# Revit family: Door-Exterior-Simpson-Nantucket-Quarter-Glass-Single
name_source: partatom
category: Doors
revit_build: Autodesk Revit Architecture 2012 (Build: 20110916_2132(x64)
units: mm (PartAtom-declared; Revit-internal decimal feet)

## types (63) — shared parameters
Assembly Code = B2030230
Construction Type = Wood
Frame = Wood - Simpson Doors - Douglas Fir
Frame Projection Ext. = 0' - 1"
Frame Projection Int. = 0' - 1"
Frame Type = Frame : Standard
Frame Width = 0' - 3"
Function = Exterior
Glass = Glass - Simpson Doors - Clear
Glass Options = http://simpsondoor.com
Horizontal Outside Muntin = No
Innerbond Double Hip-Raised Panel = No
Manufacturer = Simpsons Door Company
Number of Horizontal Muntins = 1
Ovolo Construction = Yes
Panel = Wood - Simpson Doors - Douglas Fir
Panel Stile Width = 0' - 5"
Product Documentation Link = http://www.simpsondoor.com
Product Page URL = http://www.simpsondoor.com
Thickness = 0' - 1 3/4"
Thickness Note = comes in 1 3/4" and 2 1/4" Thickness. Default is set to 1 3/4"
URL = http://www.simpsondoor.com
Vertical Outside Muntin = No
Wall Closure = By host
Wood Species = http://simpsondoor.com

## per-type parameters (varying)
| type | Bottom Rail Height | Description | Height | Middle Rail Height | Model | Muntin Width | Number of Panel Dividers | Number of Vertical Muntins | Panel Divider Width | Rough Height | Rough Width | Top Rail Height | Width | Window Height |
| 77662 Nantucket 36x80 Ovolo Flat Panel | 0' - 8 11/16" | Nantucket - Six Lite - Two Panel | 6' - 8" | 0' - 4 1/2" | 77662 | 0' - 0 3/8" | 1 | 2 | 0' - 3 1/2" | 6' - 10" | 3' - 4" | 0' - 4 15/16" | 3' - 0" | 1' - 6 1/2" |
| 77662 Nantucket 30x80 Ovolo Flat Panel | 0' - 8 11/16" | Nantucket - Six Lite - Two Panel | 6' - 8" | 0' - 4 1/2" | 77662 | 0' - 0 3/8" | 1 | 2 | 0' - 3 1/2" | 6' - 10" | 2' - 10" | 0' - 4 15/16" | 2' - 6" | 1' - 6 1/2" |
| 77662 Nantucket 32x80 Ovolo Flat Panel | 0' - 8 11/16" | Nantucket - Six Lite - Two Panel | 6' - 8" | 0' - 4 1/2" | 77662 | 0' - 0 3/8" | 1 | 2 | 0' - 3 1/2" | 6' - 10" | 3' - 0" | 0' - 4 15/16" | 2' - 8" | 1' - 6 1/2" |
| 77662 Nantucket 34x80 Ovolo Flat Panel | 0' - 8 11/16" | Nantucket - Six Lite - Two Panel | 6' - 8" | 0' - 4 1/2" | 77662 | 0' - 0 3/8" | 1 | 2 | 0' - 3 1/2" | 6' - 10" | 3' - 2" | 0' - 4 15/16" | 2' - 10" | 1' - 6 1/2" |
| 77662 Nantucket 38x80 Ovolo Flat Panel | 0' - 8 11/16" | Nantucket - Six Lite - Two Panel | 6' - 8" | 0' - 4 1/2" | 77662 | 0' - 0 3/8" | 1 | 2 | 0' - 3 1/2" | 6' - 10" | 3' - 6" | 0' - 4 15/16" | 3' - 2" | 1' - 6 1/2" |
| 77662 Nantucket 40x80 Ovolo Flat Panel | 0' - 8 11/16" | Nantucket - Six Lite - Two Panel | 6' - 8" | 0' - 4 1/2" | 77662 | 0' - 0 3/8" | 1 | 2 | 0' - 3 1/2" | 6' - 10" | 3' - 8" | 0' - 4 15/16" | 3' - 4" | 1' - 6 1/2" |
| 77662 Nantucket 42x80 Ovolo Flat Panel | 0' - 8 11/16" | Nantucket - Six Lite - Two Panel | 6' - 8" | 0' - 4 1/2" | 77662 | 0' - 0 3/8" | 1 | 2 | 0' - 3 1/2" | 6' - 10" | 3' - 10" | 0' - 4 15/16" | 3' - 6" | 1' - 6 1/2" |
| 77664 Nantucket 36x80 Ovolo Flat Panel | 0' - 8 11/16" | Nantucket - Six Lite - Two Panel | 6' - 8" | 0' - 4 1/2" | 77664 | 0' - 0 3/8" | 1 | 1 | 0' - 3 1/2" | 6' - 10" | 3' - 4" | 0' - 4 15/16" | 3' - 0" | 1' - 6 1/2" |
| 77664 Nantucket 30x80 Ovolo Flat Panel | 0' - 8 11/16" | Nantucket - Four Lite - Two Panel | 6' - 8" | 0' - 4 1/2" | 77664 | 0' - 0 3/8" | 1 | 1 | 0' - 3 1/2" | 6' - 10" | 2' - 10" | 0' - 4 15/16" | 2' - 6" | 1' - 6 1/2" |
| 77664 Nantucket 32x80 Ovolo Flat Panel | 0' - 8 11/16" | Nantucket - Four Lite - Two Panel | 6' - 8" | 0' - 4 1/2" | 77664 | 0' - 0 3/8" | 1 | 1 | 0' - 3 1/2" | 6' - 10" | 3' - 0" | 0' - 4 15/16" | 2' - 8" | 1' - 6 1/2" |
| 77664 Nantucket 34x80 Ovolo Flat Panel | 0' - 8 11/16" | Nantucket - Four Lite - Two Panel | 6' - 8" | 0' - 4 1/2" | 77664 | 0' - 0 3/8" | 1 | 1 | 0' - 3 1/2" | 6' - 10" | 3' - 2" | 0' - 4 15/16" | 2' - 10" | 1' - 6 1/2" |
| 77664 Nantucket 38x80 Ovolo Flat Panel | 0' - 8 11/16" | Nantucket - Four Lite - Two Panel | 6' - 8" | 0' - 4 1/2" | 77664 | 0' - 0 3/8" | 1 | 1 | 0' - 3 1/2" | 6' - 10" | 3' - 6" | 0' - 4 15/16" | 3' - 2" | 1' - 6 1/2" |
| 77664 Nantucket 40x80 Ovolo Flat Panel | 0' - 8 11/16" | Nantucket - Four Lite - Two Panel | 6' - 8" | 0' - 4 1/2" | 77664 | 0' - 0 3/8" | 1 | 1 | 0' - 3 1/2" | 6' - 10" | 3' - 8" | 0' - 4 15/16" | 3' - 4" | 1' - 6 1/2" |
| 77664 Nantucket 42x80 Ovolo Flat Panel | 0' - 8 11/16" | Nantucket - Four Lite - Two Panel | 6' - 8" | 0' - 4 1/2" | 77664 | 0' - 0 3/8" | 1 | 1 | 0' - 3 1/2" | 6' - 10" | 3' - 10" | 0' - 4 15/16" | 3' - 6" | 1' - 6 1/2" |
| 77860 Nantucket 36x80 Ovolo Flat Panel | 0' - 8 11/16" | Nantucket - Six Lite - Three Panel | 6' - 8" | 0' - 5 1/2" | 77860 | 0' - 1 3/4" | 2 | 2 | 0' - 1 3/4" | 6' - 10" | 3' - 4" | 0' - 4 15/16" | 3' - 0" | 1' - 6 1/2" |
| 77860 Nantucket 30x80 Ovolo Flat Panel | 0' - 8 11/16" | Nantucket - Six Lite - Three Panel | 6' - 8" | 0' - 5 1/2" | 77860 | 0' - 1 3/4" | 2 | 2 | 0' - 1 3/4" | 6' - 10" | 2' - 10" | 0' - 4 15/16" | 2' - 6" | 1' - 6 1/2" |
| 77860 Nantucket 32x80 Ovolo Flat Panel | 0' - 8 11/16" | Nantucket - Six Lite - Three Panel | 6' - 8" | 0' - 5 1/2" | 77860 | 0' - 1 3/4" | 2 | 2 | 0' - 1 3/4" | 6' - 10" | 3' - 0" | 0' - 4 15/16" | 2' - 8" | 1' - 6 1/2" |
| 77860 Nantucket 34x80 Ovolo Flat Panel | 0' - 8 11/16" | Nantucket - Six Lite - Three Panel | 6' - 8" | 0' - 5 1/2" | 77860 | 0' - 1 3/4" | 2 | 2 | 0' - 1 3/4" | 6' - 10" | 3' - 2" | 0' - 4 15/16" | 2' - 10" | 1' - 6 1/2" |
| 77860 Nantucket 38x80 Ovolo Flat Panel | 0' - 8 11/16" | Nantucket - Six Lite - Three Panel | 6' - 8" | 0' - 5 1/2" | 77860 | 0' - 1 3/4" | 2 | 2 | 0' - 1 3/4" | 6' - 10" | 3' - 6" | 0' - 4 15/16" | 3' - 2" | 1' - 6 1/2" |
| 77860 Nantucket 40x80 Ovolo Flat Panel | 0' - 8 11/16" | Nantucket - Six Lite - Three Panel | 6' - 8" | 0' - 5 1/2" | 77860 | 0' - 1 3/4" | 2 | 2 | 0' - 1 3/4" | 6' - 10" | 3' - 8" | 0' - 4 15/16" | 3' - 4" | 1' - 6 1/2" |
| 77860 Nantucket 42x80 Ovolo Flat Panel | 0' - 8 11/16" | Nantucket - Six Lite - Three Panel | 6' - 8" | 0' - 5 1/2" | 77860 | 0' - 1 3/4" | 2 | 2 | 0' - 1 3/4" | 6' - 10" | 3' - 10" | 0' - 4 15/16" | 3' - 6" | 1' - 6 1/2" |
| 77662 Nantucket 36x84 Ovolo Flat Panel | 0' - 8 11/16" | Nantucket - Six Lite - Two Panel | 7' - 0" | 0' - 4 1/2" | 77662 | 0' - 0 3/8" | 1 | 2 | 0' - 3 1/2" | 7' - 2" | 3' - 4" | 0' - 4 15/16" | 3' - 0" | 1' - 6 1/2" |
| 77662 Nantucket 30x84 Ovolo Flat Panel | 0' - 10 11/16" | Nantucket - Six Lite - Two Panel | 7' - 0" | 0' - 4 1/2" | 77662 | 0' - 0 3/8" | 1 | 2 | 0' - 3 1/2" | 7' - 2" | 2' - 10" | 0' - 6 15/16" | 2' - 6" | 1' - 6 1/2" |
| 77662 Nantucket 32x84 Ovolo Flat Panel | 0' - 10 11/16" | Nantucket - Six Lite - Two Panel | 7' - 0" | 0' - 4 1/2" | 77662 | 0' - 0 3/8" | 1 | 2 | 0' - 3 1/2" | 7' - 2" | 3' - 0" | 0' - 6 15/16" | 2' - 8" | 1' - 6 1/2" |
| 77662 Nantucket 34x84 Ovolo Flat Panel | 0' - 10 11/16" | Nantucket - Six Lite - Two Panel | 7' - 0" | 0' - 4 1/2" | 77662 | 0' - 0 3/8" | 1 | 2 | 0' - 3 1/2" | 7' - 2" | 3' - 2" | 0' - 6 15/16" | 2' - 10" | 1' - 6 1/2" |
| 77662 Nantucket 38x84 Ovolo Flat Panel | 0' - 10 11/16" | Nantucket - Six Lite - Two Panel | 7' - 0" | 0' - 4 1/2" | 77662 | 0' - 0 3/8" | 1 | 2 | 0' - 3 1/2" | 7' - 2" | 3' - 6" | 0' - 6 15/16" | 3' - 2" | 1' - 6 1/2" |
| 77662 Nantucket 40x84 Ovolo Flat Panel | 0' - 10 11/16" | Nantucket - Six Lite - Two Panel | 7' - 0" | 0' - 4 1/2" | 77662 | 0' - 0 3/8" | 1 | 2 | 0' - 3 1/2" | 7' - 2" | 3' - 8" | 0' - 6 15/16" | 3' - 4" | 1' - 6 1/2" |
| 77662 Nantucket 42x84 Ovolo Flat Panel | 0' - 10 11/16" | Nantucket - Six Lite - Two Panel | 7' - 0" | 0' - 4 1/2" | 77662 | 0' - 0 3/8" | 1 | 2 | 0' - 3 1/2" | 7' - 2" | 3' - 10" | 0' - 6 15/16" | 3' - 6" | 1' - 6 1/2" |
| 77664 Nantucket 36x84 Ovolo Flat Panel | 0' - 10 11/16" | Nantucket - Four Lite - Two Panel | 7' - 0" | 0' - 4 1/2" | 77664 | 0' - 0 3/8" | 1 | 1 | 0' - 3 1/2" | 7' - 2" | 3' - 4" | 0' - 6 15/16" | 3' - 0" | 1' - 6 1/2" |
| 77664 Nantucket 30x84 Ovolo Flat Panel | 0' - 10 11/16" | Nantucket - Four Lite - Two Panel | 7' - 0" | 0' - 4 1/2" | 77664 | 0' - 0 3/8" | 1 | 1 | 0' - 3 1/2" | 7' - 2" | 2' - 10" | 0' - 6 15/16" | 2' - 6" | 1' - 6 1/2" |
| 77664 Nantucket 32x84 Ovolo Flat Panel | 0' - 10 11/16" | Nantucket - Four Lite - Two Panel | 7' - 0" | 0' - 4 1/2" | 77664 | 0' - 0 3/8" | 1 | 1 | 0' - 3 1/2" | 7' - 2" | 3' - 0" | 0' - 6 15/16" | 2' - 8" | 1' - 6 1/2" |
| 77664 Nantucket 34x84 Ovolo Flat Panel | 0' - 10 11/16" | Nantucket - Four Lite - Two Panel | 7' - 0" | 0' - 4 1/2" | 77664 | 0' - 0 3/8" | 1 | 1 | 0' - 3 1/2" | 7' - 2" | 3' - 2" | 0' - 6 15/16" | 2' - 10" | 1' - 6 1/2" |
| 77664 Nantucket 38x84 Ovolo Flat Panel | 0' - 10 11/16" | Nantucket - Four Lite - Two Panel | 7' - 0" | 0' - 4 1/2" | 77664 | 0' - 0 3/8" | 1 | 1 | 0' - 3 1/2" | 7' - 2" | 3' - 6" | 0' - 6 15/16" | 3' - 2" | 1' - 6 1/2" |
| 77664 Nantucket 40x84 Ovolo Flat Panel | 0' - 10 11/16" | Nantucket - Four Lite - Two Panel | 7' - 0" | 0' - 4 1/2" | 77664 | 0' - 0 3/8" | 1 | 1 | 0' - 3 1/2" | 7' - 2" | 3' - 8" | 0' - 6 15/16" | 3' - 4" | 1' - 6 1/2" |
| 77664 Nantucket 42x84 Ovolo Flat Panel | 0' - 10 11/16" | Nantucket - Four Lite - Two Panel | 7' - 0" | 0' - 4 1/2" | 77664 | 0' - 0 3/8" | 1 | 1 | 0' - 3 1/2" | 7' - 2" | 3' - 10" | 0' - 6 15/16" | 3' - 6" | 1' - 6 1/2" |
| 77860 Nantucket 36x84 Ovolo Flat Panel | 0' - 10 11/16" | Nantucket - Six Lite - Three Panel | 7' - 0" | 0' - 5 1/2" | 77860 | 0' - 1 3/4" | 2 | 2 | 0' - 1 3/4" | 7' - 2" | 3' - 4" | 0' - 6 15/16" | 3' - 0" | 1' - 6 1/2" |
| 77860 Nantucket 30x84 Ovolo Flat Panel | 0' - 10 11/16" | Nantucket - Six Lite - Three Panel | 7' - 0" | 0' - 5 1/2" | 77860 | 0' - 1 3/4" | 2 | 2 | 0' - 1 3/4" | 7' - 2" | 2' - 10" | 0' - 6 15/16" | 2' - 6" | 1' - 6 1/2" |
| 77860 Nantucket 32x84 Ovolo Flat Panel | 0' - 10 11/16" | Nantucket - Six Lite - Three Panel | 7' - 0" | 0' - 5 1/2" | 77860 | 0' - 1 3/4" | 2 | 2 | 0' - 1 3/4" | 7' - 2" | 3' - 0" | 0' - 6 15/16" | 2' - 8" | 1' - 6 1/2" |
| 77860 Nantucket 34x84 Ovolo Flat Panel | 0' - 10 11/16" | Nantucket - Six Lite - Three Panel | 7' - 0" | 0' - 5 1/2" | 77860 | 0' - 1 3/4" | 2 | 2 | 0' - 1 3/4" | 7' - 2" | 3' - 2" | 0' - 6 15/16" | 2' - 10" | 1' - 6 1/2" |
| 77860 Nantucket 38x84 Ovolo Flat Panel | 0' - 10 11/16" | Nantucket - Six Lite - Three Panel | 7' - 0" | 0' - 5 1/2" | 77860 | 0' - 1 3/4" | 2 | 2 | 0' - 1 3/4" | 7' - 2" | 3' - 6" | 0' - 6 15/16" | 3' - 2" | 1' - 6 1/2" |
| 77860 Nantucket 40x84 Ovolo Flat Panel | 0' - 10 11/16" | Nantucket - Six Lite - Three Panel | 7' - 0" | 0' - 5 1/2" | 77860 | 0' - 1 3/4" | 2 | 2 | 0' - 1 3/4" | 7' - 2" | 3' - 8" | 0' - 6 15/16" | 3' - 4" | 1' - 6 1/2" |
| 77860 Nantucket 42x84 Ovolo Flat Panel | 0' - 10 11/16" | Nantucket - Six Lite - Three Panel | 7' - 0" | 0' - 5 1/2" | 77860 | 0' - 1 3/4" | 2 | 2 | 0' - 1 3/4" | 7' - 2" | 3' - 10" | 0' - 6 15/16" | 3' - 6" | 1' - 6 1/2" |
| 77662 Nantucket 36x96 Ovolo Flat Panel | 0' - 8 11/16" | Nantucket - Six Lite - Two Panel | 8' - 0" | 0' - 4 1/2" | 77662 | 0' - 0 3/8" | 1 | 2 | 0' - 3 1/2" | 8' - 2" | 3' - 4" | 0' - 4 15/16" | 3' - 0" | 2' - 3" |
| 77662 Nantucket 30x96 Ovolo Flat Panel | 0' - 8 11/16" | Nantucket - Six Lite - Two Panel | 8' - 0" | 0' - 4 1/2" | 77662 | 0' - 0 3/8" | 1 | 2 | 0' - 3 1/2" | 8' - 2" | 2' - 10" | 0' - 4 15/16" | 2' - 6" | 2' - 3" |
| 77662 Nantucket 32x96 Ovolo Flat Panel | 0' - 8 11/16" | Nantucket - Six Lite - Two Panel | 8' - 0" | 0' - 4 1/2" | 77662 | 0' - 0 3/8" | 1 | 2 | 0' - 3 1/2" | 8' - 2" | 3' - 0" | 0' - 4 15/16" | 2' - 8" | 2' - 3" |
| 77662 Nantucket 34x96 Ovolo Flat Panel | 0' - 8 11/16" | Nantucket - Six Lite - Two Panel | 8' - 0" | 0' - 4 1/2" | 77662 | 0' - 0 3/8" | 1 | 2 | 0' - 3 1/2" | 8' - 2" | 3' - 2" | 0' - 4 15/16" | 2' - 10" | 2' - 3" |
| 77662 Nantucket 38x96 Ovolo Flat Panel | 0' - 8 11/16" | Nantucket - Six Lite - Two Panel | 8' - 0" | 0' - 4 1/2" | 77662 | 0' - 0 3/8" | 1 | 2 | 0' - 3 1/2" | 8' - 2" | 3' - 6" | 0' - 4 15/16" | 3' - 2" | 2' - 3" |
| 77662 Nantucket 40x96 Ovolo Flat Panel | 0' - 8 11/16" | Nantucket - Six Lite - Two Panel | 8' - 0" | 0' - 4 1/2" | 77662 | 0' - 0 3/8" | 1 | 2 | 0' - 3 1/2" | 8' - 2" | 3' - 8" | 0' - 4 15/16" | 3' - 4" | 2' - 3" |
| 77662 Nantucket 42x96 Ovolo Flat Panel | 0' - 8 11/16" | Nantucket - Six Lite - Two Panel | 8' - 0" | 0' - 4 1/2" | 77662 | 0' - 0 3/8" | 1 | 2 | 0' - 3 1/2" | 8' - 2" | 3' - 10" | 0' - 4 15/16" | 3' - 6" | 2' - 3" |
| 77664 Nantucket 36x96 Ovolo Flat Panel | 0' - 8 11/16" | Nantucket - Four Lite - Two Panel | 8' - 0" | 0' - 4 1/2" | 77664 | 0' - 0 3/8" | 1 | 1 | 0' - 3 1/2" | 8' - 2" | 3' - 4" | 0' - 4 15/16" | 3' - 0" | 2' - 3" |
| 77664 Nantucket 30x96 Ovolo Flat Panel | 0' - 8 11/16" | Nantucket - Four Lite - Two Panel | 8' - 0" | 0' - 4 1/2" | 77664 | 0' - 0 3/8" | 1 | 1 | 0' - 3 1/2" | 8' - 2" | 2' - 10" | 0' - 4 15/16" | 2' - 6" | 2' - 3" |
| 77664 Nantucket 32x96 Ovolo Flat Panel | 0' - 8 11/16" | Nantucket - Four Lite - Two Panel | 8' - 0" | 0' - 4 1/2" | 77664 | 0' - 0 3/8" | 1 | 1 | 0' - 3 1/2" | 8' - 2" | 3' - 0" | 0' - 4 15/16" | 2' - 8" | 2' - 3" |
| 77664 Nantucket 34x96 Ovolo Flat Panel | 0' - 8 11/16" | Nantucket - Four Lite - Two Panel | 8' - 0" | 0' - 4 1/2" | 77664 | 0' - 0 3/8" | 1 | 1 | 0' - 3 1/2" | 8' - 2" | 3' - 2" | 0' - 4 15/16" | 2' - 10" | 2' - 3" |
| 77664 Nantucket 38x96 Ovolo Flat Panel | 0' - 8 11/16" | Nantucket - Four Lite - Two Panel | 8' - 0" | 0' - 4 1/2" | 77664 | 0' - 0 3/8" | 1 | 1 | 0' - 3 1/2" | 8' - 2" | 3' - 6" | 0' - 4 15/16" | 3' - 2" | 2' - 3" |
| 77664 Nantucket 40x96 Ovolo Flat Panel | 0' - 8 11/16" | Nantucket - Four Lite - Two Panel | 8' - 0" | 0' - 4 1/2" | 77664 | 0' - 0 3/8" | 1 | 1 | 0' - 3 1/2" | 8' - 2" | 3' - 8" | 0' - 4 15/16" | 3' - 4" | 2' - 3" |
| 77664 Nantucket 42x96 Ovolo Flat Panel | 0' - 8 11/16" | Nantucket - Four Lite - Two Panel | 8' - 0" | 0' - 4 1/2" | 77664 | 0' - 0 3/8" | 1 | 1 | 0' - 3 1/2" | 8' - 2" | 3' - 10" | 0' - 4 15/16" | 3' - 6" | 2' - 3" |
| 77860 Nantucket 36x96 Ovolo Flat Panel | 0' - 8 11/16" | Nantucket - Six Lite - Three Panel | 8' - 0" | 0' - 5 1/2" | 77860 | 0' - 1 3/4" | 2 | 2 | 0' - 1 3/4" | 8' - 2" | 3' - 4" | 0' - 4 15/16" | 3' - 0" | 2' - 3" |
| 77860 Nantucket 30x96 Ovolo Flat Panel | 0' - 8 11/16" | Nantucket - Six Lite - Three Panel | 8' - 0" | 0' - 5 1/2" | 77860 | 0' - 1 3/4" | 2 | 2 | 0' - 1 3/4" | 8' - 2" | 2' - 10" | 0' - 4 15/16" | 2' - 6" | 2' - 3" |
| 77860 Nantucket 32x96 Ovolo Flat Panel | 0' - 8 11/16" | Nantucket - Six Lite - Three Panel | 8' - 0" | 0' - 5 1/2" | 77860 | 0' - 1 3/4" | 2 | 2 | 0' - 1 3/4" | 8' - 2" | 3' - 0" | 0' - 4 15/16" | 2' - 8" | 2' - 3" |
| 77860 Nantucket 34x96 Ovolo Flat Panel | 0' - 8 11/16" | Nantucket - Six Lite - Three Panel | 8' - 0" | 0' - 5 1/2" | 77860 | 0' - 1 3/4" | 2 | 2 | 0' - 1 3/4" | 8' - 2" | 3' - 2" | 0' - 4 15/16" | 2' - 10" | 2' - 3" |
| 77860 Nantucket 38x96 Ovolo Flat Panel | 0' - 8 11/16" | Nantucket - Six Lite - Three Panel | 8' - 0" | 0' - 5 1/2" | 77860 | 0' - 1 3/4" | 2 | 2 | 0' - 1 3/4" | 8' - 2" | 3' - 6" | 0' - 4 15/16" | 3' - 2" | 2' - 3" |
| 77860 Nantucket 40x96 Ovolo Flat Panel | 0' - 8 11/16" | Nantucket - Six Lite - Three Panel | 8' - 0" | 0' - 5 1/2" | 77860 | 0' - 1 3/4" | 2 | 2 | 0' - 1 3/4" | 8' - 2" | 3' - 8" | 0' - 4 15/16" | 3' - 4" | 2' - 3" |
| 77860 Nantucket 42x96 Ovolo Flat Panel | 0' - 8 11/16" | Nantucket - Six Lite - Three Panel | 8' - 0" | 0' - 5 1/2" | 77860 | 0' - 1 3/4" | 2 | 2 | 0' - 1 3/4" | 8' - 2" | 3' - 10" | 0' - 4 15/16" | 3' - 6" | 2' - 3" |

## geometry (parser evidence)
native form markers: Blend x4, Sweep x24
no freeform markers — native parametric forms only
